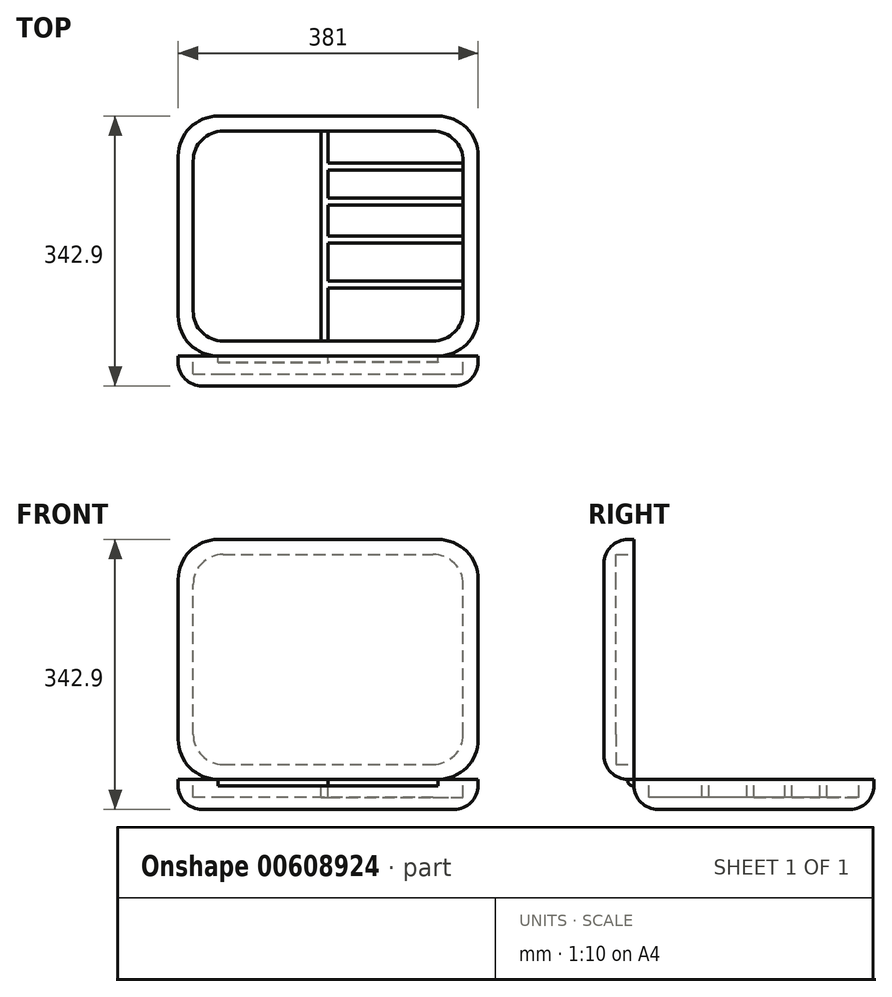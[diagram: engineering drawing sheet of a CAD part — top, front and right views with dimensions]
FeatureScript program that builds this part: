
annotation { "Feature Type Name" : "Feature", "Feature Type Description" : "" }
export const myFeature = defineFeature(function(context is Context, id is Id, definition is map)
    precondition{}
    {
        {
            var Q0;
            Q0=qCreatedBy(makeId("Top.planeOp"),FACE);
            var sketch = newSketch(context, id + "F0", { "sketchPlane" : qUnion([Q0])});
            skLineSegment(sketch, "E0.bottom", {"start": v(139.7, -152.4) * mm, "end": v(-139.7, -152.4) * mm});
            skLineSegment(sketch, "E0.top", {"start": v(139.7, 152.4) * mm, "end": v(-139.7, 152.4) * mm});
            skLineSegment(sketch, "E0.left", {"start": v(190.5, -101.6) * mm, "end": v(190.5, 101.6) * mm});
            skLineSegment(sketch, "E0.right", {"start": v(-190.5, -101.6) * mm, "end": v(-190.5, 101.6) * mm});
            skPoint(sketch, "E0.middle", {"position": v(0, 0) * mm});
            skPoint(sketch, "E1.visualSharp", {"position": v(-190.5, 152.4) * mm});
            skArc(sketch, "E1.filletArc", {"start": v(-139.7, 152.4) * mm, "mid": v(-175.62, 137.52) * mm, "end": v(-190.5, 101.6) * mm});
            skPoint(sketch, "E2.visualSharp", {"position": v(190.5, 152.4) * mm});
            skArc(sketch, "E2.filletArc", {"start": v(190.5, 101.6) * mm, "mid": v(175.62, 137.52) * mm, "end": v(139.7, 152.4) * mm});
            skPoint(sketch, "E3.visualSharp", {"position": v(190.5, -152.4) * mm});
            skArc(sketch, "E3.filletArc", {"start": v(139.7, -152.4) * mm, "mid": v(175.62, -137.52) * mm, "end": v(190.5, -101.6) * mm});
            skPoint(sketch, "E4.visualSharp", {"position": v(-190.5, -152.4) * mm});
            skArc(sketch, "E4.filletArc", {"start": v(-190.5, -101.6) * mm, "mid": v(-175.62, -137.52) * mm, "end": v(-139.7, -152.4) * mm});
            skSolve(sketch);
        }
        {
            var Q0;
            Q0=makeQuery(id+"F0.imprint","IMPRINT",FACE,{"disambiguationData":[TD([[makeQuery(id+"F0.imprint","IMPRINT",EDGE,{"derivedFrom":sQuery(id+"F0.wireOp",EDGE,"E0.bottom")}),-1.0]])]});
            extrude(context, id + "F1", {"entities" : qUnion([Q0]), "depth" : 38.1 * mm, "offsetDistance" : 25.4 * mm});
        }
        {
            var Q0;
            Q0=makeQuery(id+"F1.opExtrude","CAP_EDGE",EDGE,{"disambiguationData":[OSD([sQuery(id+"F0.wireOp",EDGE,"E0.bottom")])],"isStart":true});
            fillet(context, id + "F2", {"entities" : qUnion([Q0]), "radius" : 30.48 * mm, "tangentPropagation" : true, "allowEdgeOverflow" : false});
        }
        {
            var Q0;
            Q0=makeQuery(id+"F1.opExtrude","SWEPT_FACE",FACE,{"disambiguationData":[OSD([sQuery(id+"F0.wireOp",EDGE,"E0.bottom")])]});
            var sketch = newSketch(context, id + "F3", { "sketchPlane" : qUnion([Q0])});
            skLineSegment(sketch, "E5.bottom", {"start": v(-139.7, 342.9) * mm, "end": v(139.7, 342.9) * mm});
            skLineSegment(sketch, "E5.top", {"start": v(-139.7, 38.1) * mm, "end": v(139.7, 38.1) * mm});
            skLineSegment(sketch, "E5.left", {"start": v(-190.5, 292.1) * mm, "end": v(-190.5, 88.9) * mm});
            skLineSegment(sketch, "E5.right", {"start": v(190.5, 292.1) * mm, "end": v(190.5, 88.9) * mm});
            skPoint(sketch, "E6.visualSharp", {"position": v(-190.5, 342.9) * mm});
            skArc(sketch, "E6.filletArc", {"start": v(-139.7, 342.9) * mm, "mid": v(-175.62, 328.02) * mm, "end": v(-190.5, 292.1) * mm});
            skPoint(sketch, "E7.visualSharp", {"position": v(190.5, 342.9) * mm});
            skArc(sketch, "E7.filletArc", {"start": v(190.5, 292.1) * mm, "mid": v(175.62, 328.02) * mm, "end": v(139.7, 342.9) * mm});
            skPoint(sketch, "E8.visualSharp", {"position": v(190.5, 38.1) * mm});
            skArc(sketch, "E8.filletArc", {"start": v(139.7, 38.1) * mm, "mid": v(175.62, 52.98) * mm, "end": v(190.5, 88.9) * mm});
            skPoint(sketch, "E9.visualSharp", {"position": v(-190.5, 38.1) * mm});
            skArc(sketch, "E9.filletArc", {"start": v(-190.5, 88.9) * mm, "mid": v(-175.62, 52.98) * mm, "end": v(-139.7, 38.1) * mm});
            skSolve(sketch);
        }
        {
            var Q0;
            Q0=qSketchRegion(id+"F3",true);
            extrude(context, id + "F4", {"entities" : qUnion([Q0]), "depth" : 38.1 * mm, "offsetDistance" : 25.4 * mm});
        }
        {
            var Q0;
            Q0=makeQuery(id+"F4.opExtrude","CAP_EDGE",EDGE,{"disambiguationData":[OSD([sQuery(id+"F3.wireOp",EDGE,"E5.left")])],"isStart":false});
            fillet(context, id + "F5", {"entities" : qUnion([Q0]), "radius" : 30.48 * mm, "tangentPropagation" : true, "allowEdgeOverflow" : false});
        }
        {
            var Q0;
            Q0=qCreatedBy(makeId("Right.planeOp"),FACE);
            var sketch = newSketch(context, id + "F6", { "sketchPlane" : qUnion([Q0])});
            skArc(sketch, "E10", {"start": v(-160.02, 38.1) * mm, "mid": v(-158.64, 31.86) * mm, "end": v(-152.4, 30.48) * mm});
            skLineSegment(sketch, "E11", {"start": v(-160.02, 38.1) * mm, "end": v(-152.4, 38.1) * mm});
            skLineSegment(sketch, "E12", {"start": v(-152.4, 38.1) * mm, "end": v(-152.4, 30.48) * mm});
            skSolve(sketch);
        }
        {
            var Q0;
            Q0=qSketchRegion(id+"F6",true);
            extrude(context, id + "F7", {"entities" : qUnion([Q0]), "depth" : 139.7 * mm, "offsetDistance" : 25.4 * mm});
        }
        {
            var Q0;
            Q0=makeQuery(id+"F7.opExtrude","CAP_FACE",FACE,{"disambiguationData":[OSD([sQuery(id+"F6.wireOp",EDGE,"E10"),sQuery(id+"F6.wireOp",EDGE,"E11"),sQuery(id+"F6.wireOp",EDGE,"E12")])],"isStart":true});
            extrude(context, id + "F8", {"entities" : qUnion([Q0]), "depth" : 139.7 * mm, "offsetDistance" : 25.4 * mm});
        }
        {
            var Q0;
            Q0=makeQuery(id+"F4.opExtrude","CAP_FACE",FACE,{"disambiguationData":[OSD([sQuery(id+"F3.wireOp",EDGE,"E5.bottom"),sQuery(id+"F3.wireOp",EDGE,"E5.top"),sQuery(id+"F3.wireOp",EDGE,"E5.left"),sQuery(id+"F3.wireOp",EDGE,"E5.right"),sQuery(id+"F3.wireOp",EDGE,"E6.filletArc"),sQuery(id+"F3.wireOp",EDGE,"E7.filletArc"),sQuery(id+"F3.wireOp",EDGE,"E8.filletArc"),sQuery(id+"F3.wireOp",EDGE,"E9.filletArc")])],"isStart":true});
            var sketch = newSketch(context, id + "F9", { "sketchPlane" : qUnion([Q0])});
            skLineSegment(sketch, "E13.bottom", {"start": v(133.35, 57.15) * mm, "end": v(-133.35, 57.15) * mm});
            skLineSegment(sketch, "E13.top", {"start": v(133.35, 323.85) * mm, "end": v(-133.35, 323.85) * mm});
            skLineSegment(sketch, "E13.left", {"start": v(171.45, 95.25) * mm, "end": v(171.45, 285.75) * mm});
            skLineSegment(sketch, "E13.right", {"start": v(-171.45, 95.25) * mm, "end": v(-171.45, 285.75) * mm});
            skPoint(sketch, "E13.middle", {"position": v(0, 190.5) * mm});
            skPoint(sketch, "E14.visualSharp", {"position": v(-171.45, 323.85) * mm});
            skArc(sketch, "E14.filletArc", {"start": v(-133.35, 323.85) * mm, "mid": v(-160.3, 312.7) * mm, "end": v(-171.45, 285.75) * mm});
            skPoint(sketch, "E15.visualSharp", {"position": v(171.45, 323.85) * mm});
            skArc(sketch, "E15.filletArc", {"start": v(171.45, 285.75) * mm, "mid": v(160.3, 312.7) * mm, "end": v(133.35, 323.85) * mm});
            skPoint(sketch, "E16.visualSharp", {"position": v(171.45, 57.15) * mm});
            skArc(sketch, "E16.filletArc", {"start": v(133.35, 57.15) * mm, "mid": v(160.3, 68.3) * mm, "end": v(171.45, 95.25) * mm});
            skPoint(sketch, "E17.visualSharp", {"position": v(-171.45, 57.15) * mm});
            skArc(sketch, "E17.filletArc", {"start": v(-171.45, 95.25) * mm, "mid": v(-160.3, 68.3) * mm, "end": v(-133.35, 57.15) * mm});
            skSolve(sketch);
        }
        {
            var Q0;
            Q0=qSketchRegion(id+"F9",true);
            extrude(context, id + "F10", {"entities" : qUnion([Q0]), "operationType" : NewBodyOperationType.REMOVE, "oppositeDirection" : true, "depth" : 22.86 * mm, "offsetDistance" : 25.4 * mm});
        }
        {
            var Q0;
            Q0=makeQuery(id+"F1.opExtrude","CAP_FACE",FACE,{"disambiguationData":[OSD([sQuery(id+"F0.wireOp",EDGE,"E0.bottom"),sQuery(id+"F0.wireOp",EDGE,"E0.top"),sQuery(id+"F0.wireOp",EDGE,"E0.left"),sQuery(id+"F0.wireOp",EDGE,"E0.right"),sQuery(id+"F0.wireOp",EDGE,"E1.filletArc"),sQuery(id+"F0.wireOp",EDGE,"E2.filletArc"),sQuery(id+"F0.wireOp",EDGE,"E3.filletArc"),sQuery(id+"F0.wireOp",EDGE,"E4.filletArc")])],"isStart":false});
            var sketch = newSketch(context, id + "F11", { "sketchPlane" : qUnion([Q0])});
            skSolve(sketch);
        }
        {
            var Q0;
            Q0=makeQuery(id+"F11.imprint","IMPRINT",FACE,{"disambiguationData":[TD([[makeQuery(id+"F11.imprint","IMPRINT",EDGE,{"derivedFrom":makeQuery(id+"F1.opExtrude","CAP_EDGE",EDGE,{"disambiguationData":[OSD([sQuery(id+"F0.wireOp",EDGE,"E0.bottom")])],"isStart":false})}),-1.0]])]});
            var sketch = newSketch(context, id + "F12", { "sketchPlane" : qUnion([Q0])});
            skLineSegment(sketch, "E18", {"start": v(-171.45, 95.25) * mm, "end": v(-171.45, -95.25) * mm});
            skLineSegment(sketch, "E19", {"start": v(-133.35, -133.35) * mm, "end": v(133.35, -133.35) * mm});
            skLineSegment(sketch, "E20", {"start": v(171.45, -95.25) * mm, "end": v(171.45, 95.25) * mm});
            skLineSegment(sketch, "E21", {"start": v(133.35, 133.35) * mm, "end": v(-133.35, 133.35) * mm});
            skLineSegment(sketch, "E22", {"start": v(-171.45, 95.25) * mm, "end": v(-171.45, 0) * mm});
            skLineSegment(sketch, "E23", {"start": v(171.45, 95.25) * mm, "end": v(171.45, 0) * mm});
            skLineSegment(sketch, "E24", {"start": v(-133.35, 133.35) * mm, "end": v(0, 133.35) * mm});
            skLineSegment(sketch, "E25", {"start": v(-133.35, -133.35) * mm, "end": v(0, -133.35) * mm});
            skArc(sketch, "E26", {"start": v(-133.35, 133.35) * mm, "mid": v(-160.3, 122.2) * mm, "end": v(-171.45, 95.25) * mm});
            skArc(sketch, "E27", {"start": v(171.45, 95.25) * mm, "mid": v(160.3, 122.2) * mm, "end": v(133.35, 133.35) * mm});
            skArc(sketch, "E28", {"start": v(133.35, -133.35) * mm, "mid": v(160.3, -122.2) * mm, "end": v(171.45, -95.25) * mm});
            skArc(sketch, "E29", {"start": v(-171.45, -95.25) * mm, "mid": v(-160.3, -122.2) * mm, "end": v(-133.35, -133.35) * mm});
            skSolve(sketch);
        }
        {
            var Q0;
            Q0 = qSketchRegion(id + "F12", true);
            extrude(context, id + "F13", {"entities" : qUnion([Q0]), "operationType" : NewBodyOperationType.REMOVE, "oppositeDirection" : true, "depth" : 22.86 * mm, "offsetDistance" : 25.4 * mm});
        }
        {
            var Q0;
            Q0=makeQuery(id+"F11.imprint","IMPRINT",FACE,{"disambiguationData":[TD([[makeQuery(id+"F11.imprint","IMPRINT",EDGE,{"derivedFrom":makeQuery(id+"F1.opExtrude","CAP_EDGE",EDGE,{"disambiguationData":[OSD([sQuery(id+"F0.wireOp",EDGE,"E0.bottom")])],"isStart":false})}),-1.0]])]});
            var sketch = newSketch(context, id + "F14", { "sketchPlane" : qUnion([Q0])});
            skLineSegment(sketch, "E30", {"start": v(0, 0) * mm, "end": v(0, 133.35) * mm});
            skLineSegment(sketch, "E31", {"start": v(0, 133.35) * mm, "end": v(0, -133.35) * mm});
            skLineSegment(sketch, "E32", {"start": v(0, 92.7) * mm, "end": v(171.45, 92.71) * mm});
            skLineSegment(sketch, "E33", {"start": v(0, 48.26) * mm, "end": v(171.45, 48.26) * mm});
            skLineSegment(sketch, "E34", {"start": v(0, 0) * mm, "end": v(171.45, 0) * mm});
            skLineSegment(sketch, "E35", {"start": v(0, -57.15) * mm, "end": v(171.45, -57.15) * mm});
            skLineSegment(sketch, "E36", {"start": v(0, 83.82) * mm, "end": v(171.45, 83.82) * mm});
            skLineSegment(sketch, "E37", {"start": v(0, 39.37) * mm, "end": v(171.45, 39.37) * mm});
            skLineSegment(sketch, "E38", {"start": v(0, -8.9) * mm, "end": v(171.45, -8.89) * mm});
            skLineSegment(sketch, "E39", {"start": v(0, -66.04) * mm, "end": v(171.45, -66.04) * mm});
            skLineSegment(sketch, "E40", {"start": v(-8.9, 133.35) * mm, "end": v(-8.89, -133.35) * mm});
            skLineSegment(sketch, "E41", {"start": v(-8.9, 133.35) * mm, "end": v(0, 133.35) * mm});
            skLineSegment(sketch, "E42", {"start": v(-8.89, -133.35) * mm, "end": v(0, -133.35) * mm});
            skLineSegment(sketch, "E43", {"start": v(171.45, 92.71) * mm, "end": v(171.45, 83.82) * mm});
            skLineSegment(sketch, "E44", {"start": v(171.45, 48.26) * mm, "end": v(171.45, 39.37) * mm});
            skLineSegment(sketch, "E45", {"start": v(171.45, 0) * mm, "end": v(171.45, -8.89) * mm});
            skLineSegment(sketch, "E46", {"start": v(171.45, -57.15) * mm, "end": v(171.45, -66.04) * mm});
            skSolve(sketch);
        }
        {
            var Q0;
            Q0 = qSketchRegion(id + "F14", true);
            extrude(context, id + "F15", {"entities" : qUnion([Q0]), "oppositeDirection" : true, "depth" : 22.86 * mm, "offsetDistance" : 25.4 * mm});
        }
    });
